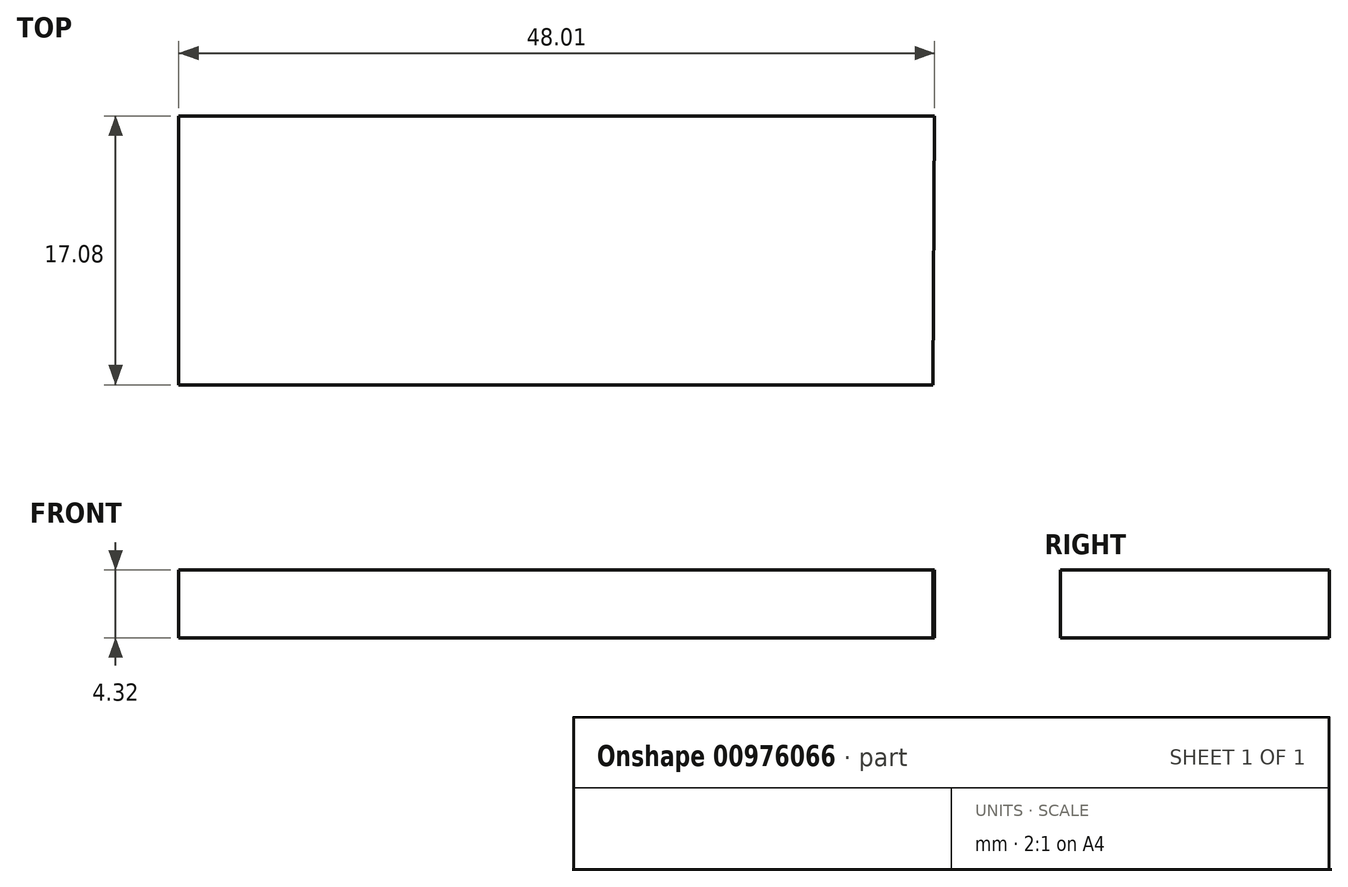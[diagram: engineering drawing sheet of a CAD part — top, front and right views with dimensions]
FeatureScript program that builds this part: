
annotation { "Feature Type Name" : "Feature", "Feature Type Description" : "" }
export const myFeature = defineFeature(function(context is Context, id is Id, definition is map)
    precondition{}
    {
        {
            var Q0;
            Q0=qCreatedBy(makeId("Top.planeOp"),FACE);
            var sketch = newSketch(context, id + "F0", { "sketchPlane" : qUnion([Q0])});
            skLineSegment(sketch, "E0", {"start": v(22.59, 9.65) * mm, "end": v(-25.42, 9.65) * mm});
            skLineSegment(sketch, "E1", {"start": v(-25.42, 9.65) * mm, "end": v(-25.42, -7.43) * mm});
            skLineSegment(sketch, "E2", {"start": v(-25.42, -7.43) * mm, "end": v(22.47, -7.43) * mm});
            skLineSegment(sketch, "E3", {"start": v(22.59, 9.65) * mm, "end": v(22.47, -7.43) * mm});
            skSolve(sketch);
        }
        {
            var Q0;
            Q0 = qSketchRegion(id + "F0", true);
            extrude(context, id + "F1", {"entities" : qUnion([Q0]), "depth" : 4.32 * mm, "offsetDistance" : 25.4 * mm});
        }
    });
